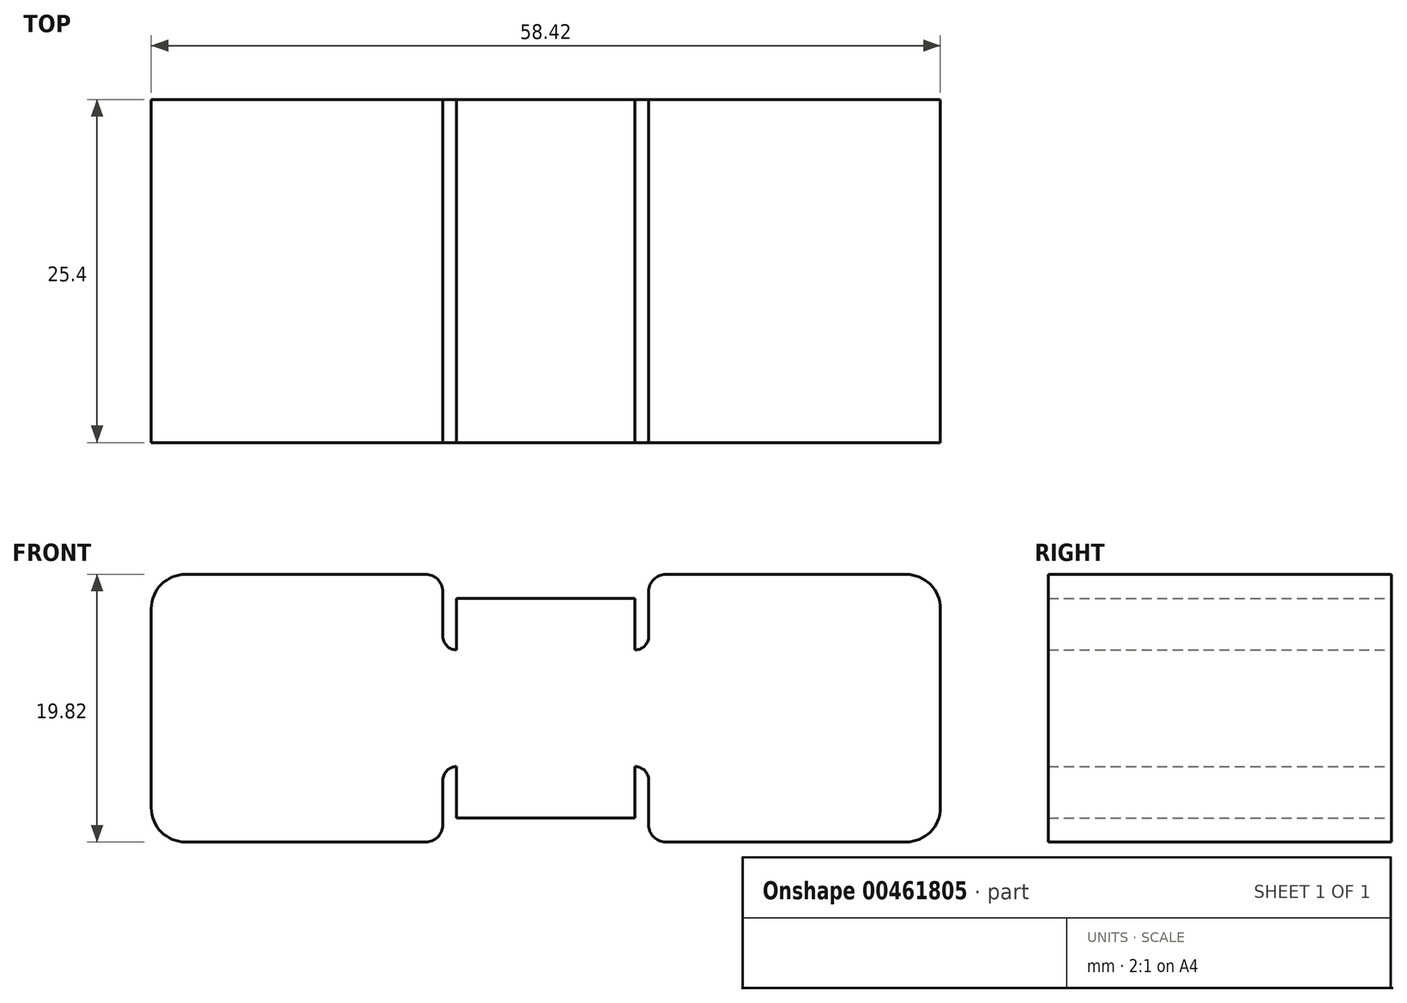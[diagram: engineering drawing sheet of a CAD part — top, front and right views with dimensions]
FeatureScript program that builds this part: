
annotation { "Feature Type Name" : "Feature", "Feature Type Description" : "" }
export const myFeature = defineFeature(function(context is Context, id is Id, definition is map)
    precondition{}
    {
        {
            var Q0;
            Q0=qCreatedBy(makeId("Front.planeOp"),FACE);
            var sketch = newSketch(context, id + "F0", { "sketchPlane" : qUnion([Q0])});
            skLineSegment(sketch, "E0", {"start": v(0, 0) * mm, "end": v(0, 8.13) * mm});
            skLineSegment(sketch, "E1", {"start": v(0, 0) * mm, "end": v(-29.21, 0) * mm});
            skLineSegment(sketch, "E2", {"start": v(-29.21, 0) * mm, "end": v(-29.21, 7.37) * mm});
            skLineSegment(sketch, "E3", {"start": v(0, 8.13) * mm, "end": v(-6.6, 8.13) * mm});
            skLineSegment(sketch, "E4", {"start": v(-26.67, 9.9) * mm, "end": v(-8.89, 9.9) * mm});
            skPoint(sketch, "E5.endSnap0", {"position": v(0, 4.06) * mm});
            skLineSegment(sketch, "E6", {"start": v(-7.62, 8.64) * mm, "end": v(-7.62, 5.33) * mm});
            skLineSegment(sketch, "E7", {"start": v(-6.6, 4.32) * mm, "end": v(-6.6, 4.32) * mm});
            skPoint(sketch, "E8.visualSharp", {"position": v(-29.21, 9.9) * mm});
            skArc(sketch, "E8.filletArc", {"start": v(-26.67, 9.9) * mm, "mid": v(-28.47, 9.16) * mm, "end": v(-29.21, 7.37) * mm});
            skPoint(sketch, "E9.visualSharp", {"position": v(-7.62, 9.9) * mm});
            skArc(sketch, "E9.filletArc", {"start": v(-7.62, 8.64) * mm, "mid": v(-8, 9.53) * mm, "end": v(-8.89, 9.9) * mm});
            skLineSegment(sketch, "E10", {"start": v(-6.6, 8.13) * mm, "end": v(-6.6, 4.32) * mm});
            skPoint(sketch, "E11.visualSharp", {"position": v(-7.62, 4.32) * mm});
            skArc(sketch, "E11.filletArc", {"start": v(-7.62, 5.33) * mm, "mid": v(-7.32, 4.62) * mm, "end": v(-6.6, 4.32) * mm});
            skLineSegment(sketch, "E12.MirrorCS", {"start": v(0, 8.13) * mm, "end": v(6.6, 8.13) * mm});
            skLineSegment(sketch, "E13.MirrorCS", {"start": v(0, 0) * mm, "end": v(29.21, 0) * mm});
            skPoint(sketch, "E14.MirrorP", {"position": v(7.62, 4.32) * mm});
            skLineSegment(sketch, "E15.MirrorCS", {"start": v(7.62, 8.64) * mm, "end": v(7.62, 5.33) * mm});
            skArc(sketch, "E16.MirrorCS", {"start": v(7.62, 5.33) * mm, "mid": v(7.32, 4.62) * mm, "end": v(6.6, 4.32) * mm});
            skArc(sketch, "E17.MirrorCS", {"start": v(7.62, 8.64) * mm, "mid": v(8, 9.53) * mm, "end": v(8.89, 9.9) * mm});
            skLineSegment(sketch, "E18.MirrorCS", {"start": v(26.67, 9.9) * mm, "end": v(8.89, 9.9) * mm});
            skArc(sketch, "E19.MirrorCS", {"start": v(26.67, 9.9) * mm, "mid": v(28.47, 9.16) * mm, "end": v(29.21, 7.37) * mm});
            skLineSegment(sketch, "E20.MirrorCS", {"start": v(29.21, 0) * mm, "end": v(29.21, 7.37) * mm});
            skLineSegment(sketch, "E21.MirrorCS", {"start": v(6.6, 8.13) * mm, "end": v(6.6, 4.32) * mm});
            skPoint(sketch, "E22.MirrorP", {"position": v(7.62, 9.9) * mm});
            skLineSegment(sketch, "E23.MirrorCS", {"start": v(26.67, -9.9) * mm, "end": v(8.89, -9.9) * mm});
            skLineSegment(sketch, "E24.MirrorCS", {"start": v(7.62, -8.64) * mm, "end": v(7.62, -5.33) * mm});
            skPoint(sketch, "E25.MirrorP", {"position": v(7.62, -9.9) * mm});
            skArc(sketch, "E26.MirrorCS", {"start": v(7.62, -8.64) * mm, "mid": v(8, -9.53) * mm, "end": v(8.89, -9.9) * mm});
            skLineSegment(sketch, "E27.MirrorCS", {"start": v(0, -8.13) * mm, "end": v(6.6, -8.13) * mm});
            skPoint(sketch, "E28.MirrorP", {"position": v(0, -4.06) * mm});
            skLineSegment(sketch, "E29.MirrorCS", {"start": v(0, 0) * mm, "end": v(0, -8.13) * mm});
            skLineSegment(sketch, "E30.MirrorCS", {"start": v(29.21, 0) * mm, "end": v(29.21, -7.37) * mm});
            skArc(sketch, "E31.MirrorCS", {"start": v(26.67, -9.9) * mm, "mid": v(28.47, -9.16) * mm, "end": v(29.21, -7.37) * mm});
            skLineSegment(sketch, "E32.MirrorCS", {"start": v(6.6, -8.13) * mm, "end": v(6.6, -4.32) * mm});
            skPoint(sketch, "E33.MirrorP", {"position": v(7.62, -4.32) * mm});
            skArc(sketch, "E34.MirrorCS", {"start": v(-7.62, -5.33) * mm, "mid": v(-7.32, -4.62) * mm, "end": v(-6.6, -4.32) * mm});
            skLineSegment(sketch, "E35.MirrorCS", {"start": v(-6.6, -8.13) * mm, "end": v(-6.6, -4.32) * mm});
            skLineSegment(sketch, "E36.MirrorCS", {"start": v(0, -8.13) * mm, "end": v(-6.6, -8.13) * mm});
            skLineSegment(sketch, "E37.MirrorCS", {"start": v(-7.62, -8.64) * mm, "end": v(-7.62, -5.33) * mm});
            skArc(sketch, "E38.MirrorCS", {"start": v(-7.62, -8.64) * mm, "mid": v(-8, -9.53) * mm, "end": v(-8.89, -9.9) * mm});
            skLineSegment(sketch, "E39.MirrorCS", {"start": v(-26.67, -9.9) * mm, "end": v(-8.89, -9.9) * mm});
            skArc(sketch, "E40.MirrorCS", {"start": v(-26.67, -9.9) * mm, "mid": v(-28.47, -9.16) * mm, "end": v(-29.21, -7.37) * mm});
            skLineSegment(sketch, "E41.MirrorCS", {"start": v(-29.21, 0) * mm, "end": v(-29.21, -7.37) * mm});
            skArc(sketch, "E42.MirrorCS", {"start": v(7.62, -5.33) * mm, "mid": v(7.32, -4.62) * mm, "end": v(6.6, -4.32) * mm});
            skSolve(sketch);
        }
        {
            var Q0;
            Q0=makeQuery(id+"F0.imprint","IMPRINT",FACE,{"disambiguationData":[TD([[makeQuery(id+"F0.imprint","IMPRINT",EDGE,{"derivedFrom":sQuery(id+"F0.wireOp",EDGE,"E0")}),1.0]])]});
            var Q1;
            Q1=makeQuery(id+"F0.imprint","IMPRINT",FACE,{"disambiguationData":[TD([[makeQuery(id+"F0.imprint","IMPRINT",EDGE,{"derivedFrom":sQuery(id+"F0.wireOp",EDGE,"E0")}),-1.0]])]});
            var Q2;
            Q2=makeQuery(id+"F0.imprint","IMPRINT",FACE,{"disambiguationData":[TD([[makeQuery(id+"F0.imprint","IMPRINT",EDGE,{"derivedFrom":sQuery(id+"F0.wireOp",EDGE,"E13.MirrorCS")}),-1.0]])]});
            var Q3;
            Q3=makeQuery(id+"F0.imprint","IMPRINT",FACE,{"disambiguationData":[TD([[makeQuery(id+"F0.imprint","IMPRINT",EDGE,{"derivedFrom":sQuery(id+"F0.wireOp",EDGE,"E1")}),1.0]])]});
            extrude(context, id + "F1", {"entities" : qUnion([Q0, Q1, Q2, Q3]), "depth" : 25.4 * mm});
        }
    });
